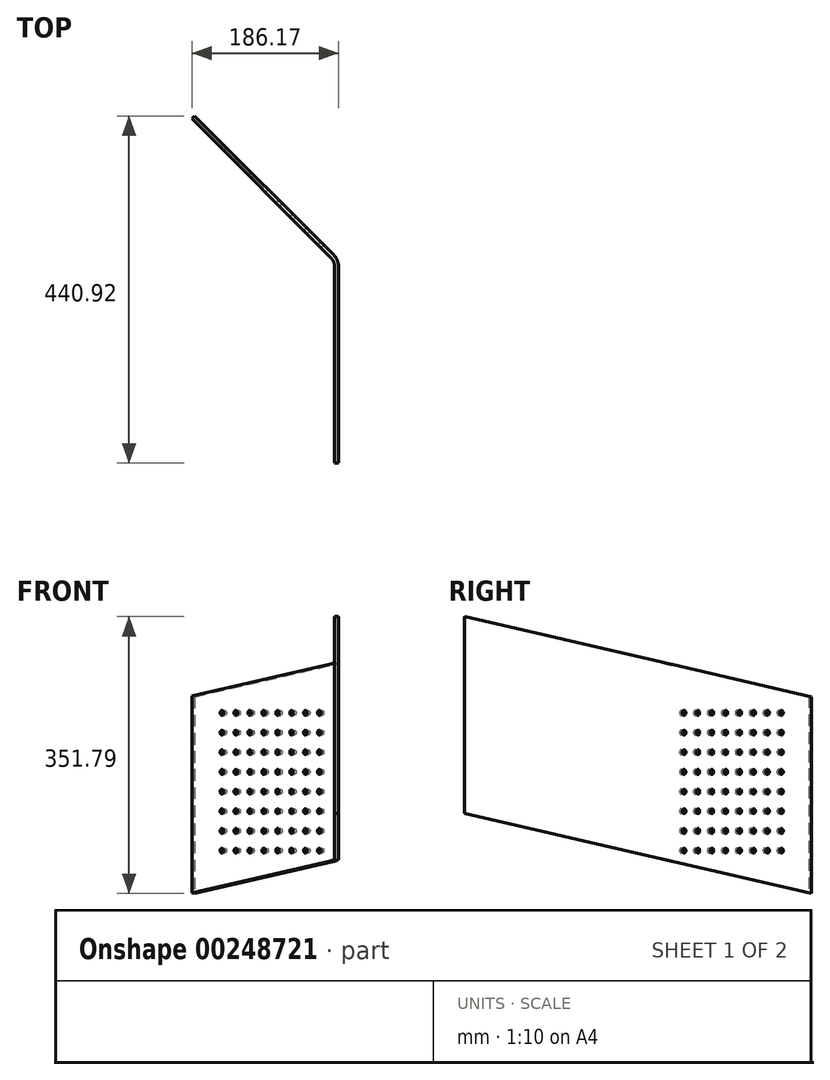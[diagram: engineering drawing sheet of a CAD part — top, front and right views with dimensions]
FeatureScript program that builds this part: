
annotation { "Feature Type Name" : "Feature", "Feature Type Description" : "" }
export const myFeature = defineFeature(function(context is Context, id is Id, definition is map)
    precondition{}
    {
        {
            var Q0;
            Q0=qCreatedBy(makeId("Right.planeOp"),FACE);
            var sketch = newSketch(context, id + "F0", { "sketchPlane" : qUnion([Q0])});
            skLineSegment(sketch, "E0", {"start": v(0, 0) * mm, "end": v(800, -184.7) * mm});
            skLineSegment(sketch, "E1", {"start": v(800, -184.7) * mm, "end": v(800, -434.7) * mm});
            skLineSegment(sketch, "E2", {"start": v(800, -434.7) * mm, "end": v(0, -250) * mm});
            skLineSegment(sketch, "E3", {"start": v(0, -250) * mm, "end": v(0, 0) * mm});
            skSolve(sketch);
        }
        {
            var Q0;
            Q0=qCreatedBy(makeId("Top.planeOp"),FACE);
            var sketch = newSketch(context, id + "F1", { "sketchPlane" : qUnion([Q0])});
            skLineSegment(sketch, "E4", {"start": v(5, 0) * mm, "end": v(5, 250) * mm});
            skLineSegment(sketch, "E5", {"start": v(-0.86, 264.14) * mm, "end": v(-177.63, 440.92) * mm});
            skPoint(sketch, "E6.visualSharp", {"position": v(5, 258.28) * mm});
            skArc(sketch, "E6.filletArc", {"start": v(5, 250) * mm, "mid": v(3.48, 257.65) * mm, "end": v(-0.86, 264.14) * mm});
            skLineSegment(sketch, "E7", {"start": v(-177.63, 440.92) * mm, "end": v(-181.17, 437.38) * mm});
            skLineSegment(sketch, "E8", {"start": v(-181.17, 437.38) * mm, "end": v(-4.4, 260.6) * mm});
            skLineSegment(sketch, "E9", {"start": v(0, 250) * mm, "end": v(0, 0) * mm});
            skLineSegment(sketch, "E10", {"start": v(0, 0) * mm, "end": v(5, 0) * mm});
            skPoint(sketch, "E11.visualSharp", {"position": v(0, 0) * mm});
            skArc(sketch, "E11.filletArc", {"start": v(0, 250) * mm, "mid": v(-1.14, 255.74) * mm, "end": v(-4.4, 260.6) * mm});
            skPoint(sketch, "E12", {"position": v(1.17, 0.48) * mm});
            skSolve(sketch);
        }
        {
            var Q0;
            Q0 = qSketchRegion(id + "F1", true);
            extrude(context, id + "F2", {"entities" : qUnion([Q0]), "endBound" : BoundingType.SYMMETRIC, "depth" : 1000 * mm});
        }
        {
            var Q0;
            Q0 = qSketchRegion(id + "F0", true);
            extrude(context, id + "F3", {"entities" : qUnion([Q0]), "operationType" : NewBodyOperationType.INTERSECT, "endBound" : BoundingType.SYMMETRIC, "oppositeDirection" : true, "depth" : 500 * mm});
        }
        {
            var Q0;
            Q0=makeQuery(id+"F2.opExtrude","SWEPT_FACE",FACE,{"disambiguationData":[OSD([sQuery(id+"F1.wireOp",EDGE,"E5")])]});
            var sketch = newSketch(context, id + "F4", { "sketchPlane" : qUnion([Q0])});
            skPoint(sketch, "E13", {"position": v(208.5, -122.3) * mm});
            skPoint(sketch, "E14.0.1.0", {"position": v(208.5, -147.3) * mm});
            skPoint(sketch, "E14.0.2.0", {"position": v(208.5, -172.3) * mm});
            skPoint(sketch, "E14.0.3.0", {"position": v(208.5, -197.3) * mm});
            skPoint(sketch, "E14.0.4.0", {"position": v(208.5, -222.3) * mm});
            skPoint(sketch, "E14.0.5.0", {"position": v(208.5, -247.3) * mm});
            skPoint(sketch, "E14.0.6.0", {"position": v(208.5, -272.3) * mm});
            skPoint(sketch, "E14.0.7.0", {"position": v(208.5, -297.3) * mm});
            skPoint(sketch, "E14.1.0.0", {"position": v(233.5, -122.3) * mm});
            skPoint(sketch, "E14.1.1.0", {"position": v(233.5, -147.3) * mm});
            skPoint(sketch, "E14.1.2.0", {"position": v(233.5, -172.3) * mm});
            skPoint(sketch, "E14.1.3.0", {"position": v(233.5, -197.3) * mm});
            skPoint(sketch, "E14.1.4.0", {"position": v(233.5, -222.3) * mm});
            skPoint(sketch, "E14.1.5.0", {"position": v(233.5, -247.3) * mm});
            skPoint(sketch, "E14.1.6.0", {"position": v(233.5, -272.3) * mm});
            skPoint(sketch, "E14.1.7.0", {"position": v(233.5, -297.3) * mm});
            skPoint(sketch, "E14.2.0.0", {"position": v(258.5, -122.3) * mm});
            skPoint(sketch, "E14.2.1.0", {"position": v(258.5, -147.3) * mm});
            skPoint(sketch, "E14.2.2.0", {"position": v(258.5, -172.3) * mm});
            skPoint(sketch, "E14.2.3.0", {"position": v(258.5, -197.3) * mm});
            skPoint(sketch, "E14.2.4.0", {"position": v(258.5, -222.3) * mm});
            skPoint(sketch, "E14.2.5.0", {"position": v(258.5, -247.3) * mm});
            skPoint(sketch, "E14.2.6.0", {"position": v(258.5, -272.3) * mm});
            skPoint(sketch, "E14.2.7.0", {"position": v(258.5, -297.3) * mm});
            skPoint(sketch, "E14.3.0.0", {"position": v(283.5, -122.3) * mm});
            skPoint(sketch, "E14.3.1.0", {"position": v(283.5, -147.3) * mm});
            skPoint(sketch, "E14.3.2.0", {"position": v(283.5, -172.3) * mm});
            skPoint(sketch, "E14.3.3.0", {"position": v(283.5, -197.3) * mm});
            skPoint(sketch, "E14.3.4.0", {"position": v(283.5, -222.3) * mm});
            skPoint(sketch, "E14.3.5.0", {"position": v(283.5, -247.3) * mm});
            skPoint(sketch, "E14.3.6.0", {"position": v(283.5, -272.3) * mm});
            skPoint(sketch, "E14.3.7.0", {"position": v(283.5, -297.3) * mm});
            skPoint(sketch, "E14.4.0.0", {"position": v(308.5, -122.3) * mm});
            skPoint(sketch, "E14.4.1.0", {"position": v(308.5, -147.3) * mm});
            skPoint(sketch, "E14.4.2.0", {"position": v(308.5, -172.3) * mm});
            skPoint(sketch, "E14.4.3.0", {"position": v(308.5, -197.3) * mm});
            skPoint(sketch, "E14.4.4.0", {"position": v(308.5, -222.3) * mm});
            skPoint(sketch, "E14.4.5.0", {"position": v(308.5, -247.3) * mm});
            skPoint(sketch, "E14.4.6.0", {"position": v(308.5, -272.3) * mm});
            skPoint(sketch, "E14.4.7.0", {"position": v(308.5, -297.3) * mm});
            skPoint(sketch, "E14.5.0.0", {"position": v(333.5, -122.3) * mm});
            skPoint(sketch, "E14.5.1.0", {"position": v(333.5, -147.3) * mm});
            skPoint(sketch, "E14.5.2.0", {"position": v(333.5, -172.3) * mm});
            skPoint(sketch, "E14.5.3.0", {"position": v(333.5, -197.3) * mm});
            skPoint(sketch, "E14.5.4.0", {"position": v(333.5, -222.3) * mm});
            skPoint(sketch, "E14.5.5.0", {"position": v(333.5, -247.3) * mm});
            skPoint(sketch, "E14.5.6.0", {"position": v(333.5, -272.3) * mm});
            skPoint(sketch, "E14.5.7.0", {"position": v(333.5, -297.3) * mm});
            skPoint(sketch, "E14.6.0.0", {"position": v(358.5, -122.3) * mm});
            skPoint(sketch, "E14.6.1.0", {"position": v(358.5, -147.3) * mm});
            skPoint(sketch, "E14.6.2.0", {"position": v(358.5, -172.3) * mm});
            skPoint(sketch, "E14.6.3.0", {"position": v(358.5, -197.3) * mm});
            skPoint(sketch, "E14.6.4.0", {"position": v(358.5, -222.3) * mm});
            skPoint(sketch, "E14.6.5.0", {"position": v(358.5, -247.3) * mm});
            skPoint(sketch, "E14.6.6.0", {"position": v(358.5, -272.3) * mm});
            skPoint(sketch, "E14.6.7.0", {"position": v(358.5, -297.3) * mm});
            skPoint(sketch, "E14.7.0.0", {"position": v(383.5, -122.3) * mm});
            skPoint(sketch, "E14.7.1.0", {"position": v(383.5, -147.3) * mm});
            skPoint(sketch, "E14.7.2.0", {"position": v(383.5, -172.3) * mm});
            skPoint(sketch, "E14.7.3.0", {"position": v(383.5, -197.3) * mm});
            skPoint(sketch, "E14.7.4.0", {"position": v(383.5, -222.3) * mm});
            skPoint(sketch, "E14.7.5.0", {"position": v(383.5, -247.3) * mm});
            skPoint(sketch, "E14.7.6.0", {"position": v(383.5, -272.3) * mm});
            skPoint(sketch, "E14.7.7.0", {"position": v(383.5, -297.3) * mm});
            skLineSegment(sketch, "E14.direction1", {"start": v(208.5, -122.3) * mm, "end": v(233.5, -122.3) * mm, "construction": true});
            skLineSegment(sketch, "E14.direction2", {"start": v(208.5, -122.3) * mm, "end": v(208.5, -147.3) * mm, "construction": true});
            skSolve(sketch);
        }
        {
            var Q0;
            Q0=sQuery(id+"F4.wireOp",VERTEX,"E14.direction1.start");
            var Q1;
            Q1=sQuery(id+"F4.wireOp",VERTEX,"E14.1.0.0");
            var Q2;
            Q2=sQuery(id+"F4.wireOp",VERTEX,"E14.2.0.0");
            var Q3;
            Q3=sQuery(id+"F4.wireOp",VERTEX,"E14.3.0.0");
            var Q4;
            Q4=sQuery(id+"F4.wireOp",VERTEX,"E14.4.0.0");
            var Q5;
            Q5=sQuery(id+"F4.wireOp",VERTEX,"E14.direction2.end");
            var Q6;
            Q6=sQuery(id+"F4.wireOp",VERTEX,"E14.4.1.0");
            var Q7;
            Q7=sQuery(id+"F4.wireOp",VERTEX,"E14.2.2.0");
            var Q8;
            Q8=sQuery(id+"F4.wireOp",VERTEX,"E14.2.1.0");
            var Q9;
            Q9=sQuery(id+"F4.wireOp",VERTEX,"E14.2.7.0");
            var Q10;
            Q10=sQuery(id+"F4.wireOp",VERTEX,"E14.4.5.0");
            var Q11;
            Q11=sQuery(id+"F4.wireOp",VERTEX,"E14.0.2.0");
            var Q12;
            Q12=sQuery(id+"F4.wireOp",VERTEX,"E14.0.3.0");
            var Q13;
            Q13=sQuery(id+"F4.wireOp",VERTEX,"E14.0.5.0");
            var Q14;
            Q14=sQuery(id+"F4.wireOp",VERTEX,"E14.0.7.0");
            var Q15;
            Q15=sQuery(id+"F4.wireOp",VERTEX,"E14.4.6.0");
            var Q16;
            Q16=sQuery(id+"F4.wireOp",VERTEX,"E14.2.4.0");
            var Q17;
            Q17=sQuery(id+"F4.wireOp",VERTEX,"E14.7.0.0");
            var Q18;
            Q18=sQuery(id+"F4.wireOp",VERTEX,"E14.2.6.0");
            var Q19;
            Q19=sQuery(id+"F4.wireOp",VERTEX,"E14.5.3.0");
            var Q20;
            Q20=sQuery(id+"F4.wireOp",VERTEX,"E14.6.6.0");
            var Q21;
            Q21=sQuery(id+"F4.wireOp",VERTEX,"E14.4.3.0");
            var Q22;
            Q22=sQuery(id+"F4.wireOp",VERTEX,"E14.2.3.0");
            var Q23;
            Q23=sQuery(id+"F4.wireOp",VERTEX,"E14.3.1.0");
            var Q24;
            Q24=sQuery(id+"F4.wireOp",VERTEX,"E14.3.4.0");
            var Q25;
            Q25=sQuery(id+"F4.wireOp",VERTEX,"E14.1.4.0");
            var Q26;
            Q26=sQuery(id+"F4.wireOp",VERTEX,"E14.5.2.0");
            var Q27;
            Q27=sQuery(id+"F4.wireOp",VERTEX,"E14.3.2.0");
            var Q28;
            Q28=sQuery(id+"F4.wireOp",VERTEX,"E14.1.6.0");
            var Q29;
            Q29=sQuery(id+"F4.wireOp",VERTEX,"E14.2.5.0");
            var Q30;
            Q30=sQuery(id+"F4.wireOp",VERTEX,"E14.7.7.0");
            var Q31;
            Q31=sQuery(id+"F4.wireOp",VERTEX,"E14.3.7.0");
            var Q32;
            Q32=sQuery(id+"F4.wireOp",VERTEX,"E14.5.7.0");
            var Q33;
            Q33=sQuery(id+"F4.wireOp",VERTEX,"E14.1.7.0");
            var Q34;
            Q34=sQuery(id+"F4.wireOp",VERTEX,"E14.7.2.0");
            var Q35;
            Q35=sQuery(id+"F4.wireOp",VERTEX,"E14.7.5.0");
            var Q36;
            Q36=sQuery(id+"F4.wireOp",VERTEX,"E14.7.1.0");
            var Q37;
            Q37=sQuery(id+"F4.wireOp",VERTEX,"E14.5.5.0");
            var Q38;
            Q38=sQuery(id+"F4.wireOp",VERTEX,"E14.4.2.0");
            var Q39;
            Q39=sQuery(id+"F4.wireOp",VERTEX,"E14.5.1.0");
            var Q40;
            Q40=sQuery(id+"F4.wireOp",VERTEX,"E14.3.5.0");
            var Q41;
            Q41=sQuery(id+"F4.wireOp",VERTEX,"E14.1.5.0");
            var Q42;
            Q42=sQuery(id+"F4.wireOp",VERTEX,"E14.6.5.0");
            var Q43;
            Q43=sQuery(id+"F4.wireOp",VERTEX,"E14.7.6.0");
            var Q44;
            Q44=sQuery(id+"F4.wireOp",VERTEX,"E14.3.6.0");
            var Q45;
            Q45=sQuery(id+"F4.wireOp",VERTEX,"E14.5.6.0");
            var Q46;
            Q46=sQuery(id+"F4.wireOp",VERTEX,"E14.6.3.0");
            var Q47;
            Q47=sQuery(id+"F4.wireOp",VERTEX,"E14.7.4.0");
            var Q48;
            Q48=sQuery(id+"F4.wireOp",VERTEX,"E14.1.1.0");
            var Q49;
            Q49=sQuery(id+"F4.wireOp",VERTEX,"E14.5.4.0");
            var Q50;
            Q50=sQuery(id+"F4.wireOp",VERTEX,"E14.4.7.0");
            var Q51;
            Q51=sQuery(id+"F4.wireOp",VERTEX,"E14.1.2.0");
            var Q52;
            Q52=sQuery(id+"F4.wireOp",VERTEX,"E14.1.3.0");
            var Q53;
            Q53=sQuery(id+"F4.wireOp",VERTEX,"E14.6.1.0");
            var Q54;
            Q54=sQuery(id+"F4.wireOp",VERTEX,"E14.6.4.0");
            var Q55;
            Q55=sQuery(id+"F4.wireOp",VERTEX,"E14.3.3.0");
            var Q56;
            Q56=sQuery(id+"F4.wireOp",VERTEX,"E14.6.2.0");
            var Q57;
            Q57=sQuery(id+"F4.wireOp",VERTEX,"E14.7.3.0");
            var Q58;
            Q58=sQuery(id+"F4.wireOp",VERTEX,"E14.4.4.0");
            var Q59;
            Q59=sQuery(id+"F4.wireOp",VERTEX,"E14.0.6.0");
            var Q60;
            Q60=sQuery(id+"F4.wireOp",VERTEX,"E14.6.7.0");
            var Q61;
            Q61=sQuery(id+"F4.wireOp",VERTEX,"E14.0.4.0");
            var Q62;
            Q62=sQuery(id+"F4.wireOp",VERTEX,"E14.6.0.0");
            var Q63;
            Q63=sQuery(id+"F4.wireOp",VERTEX,"E14.5.0.0");
            var Q64;
            Q64=makeQuery(id+"F2.opExtrude","SWEPT_BODY",BODY,{"disambiguationData":[OSD([sQuery(id+"F1.wireOp",EDGE,"E4"),sQuery(id+"F1.wireOp",EDGE,"E5"),sQuery(id+"F1.wireOp",EDGE,"E6.filletArc"),sQuery(id+"F1.wireOp",EDGE,"E7"),sQuery(id+"F1.wireOp",EDGE,"E8"),sQuery(id+"F1.wireOp",EDGE,"E9"),sQuery(id+"F1.wireOp",EDGE,"E10"),sQuery(id+"F1.wireOp",EDGE,"E11.filletArc")])]});
            hole(context, id + "F5", {"style" : HoleStyle.SIMPLE, "endStyle" : HoleEndStyle.BLIND, "holeDiameter" : 6 * mm, "holeDepth" : 12 * mm, "tappedDepth" : 12 * mm, "tapClearance" : 3, "locations" : qUnion([Q0, Q1, Q2, Q3, Q4, Q5, Q6, Q7, Q8, Q9, Q10, Q11, Q12, Q13, Q14, Q15, Q16, Q17, Q18, Q19, Q20, Q21, Q22, Q23, Q24, Q25, Q26, Q27, Q28, Q29, Q30, Q31, Q32, Q33, Q34, Q35, Q36, Q37, Q38, Q39, Q40, Q41, Q42, Q43, Q44, Q45, Q46, Q47, Q48, Q49, Q50, Q51, Q52, Q53, Q54, Q55, Q56, Q57, Q58, Q59, Q60, Q61, Q62, Q63]), "scope" : qUnion([Q64])});
        }
    });
